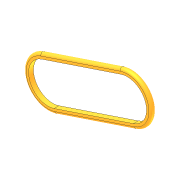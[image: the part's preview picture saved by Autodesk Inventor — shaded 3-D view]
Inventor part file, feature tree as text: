
AUTODESK INVENTOR PART (.ipt)
format: ipt  version: 2012 (Build 160160000, 160)  size: 103,936 bytes
history: native  units: in
note: dims shown in document units (in); Inventor stores cm internally (conversion verified against a paired STEP export)
features: extrude x1, fillet x1, sketch x1
ambient origin geometry x8: Origin, YZ Plane, XZ Plane, XY Plane, X Axis, Y Axis, Z Axis, Center Point
bodies: Solid1 (feature_tree)
feature tree (3):
  extrude  "Extrusion1"  Depth=3.25in
  fillet  "Fillet1"  Radius=0.1875in
  sketch  "Sketch1"  dims[d0=0.75in d1=3.25in d2=0.1875in d3=0.1875in d4=0.0in d5=0.0938in]
